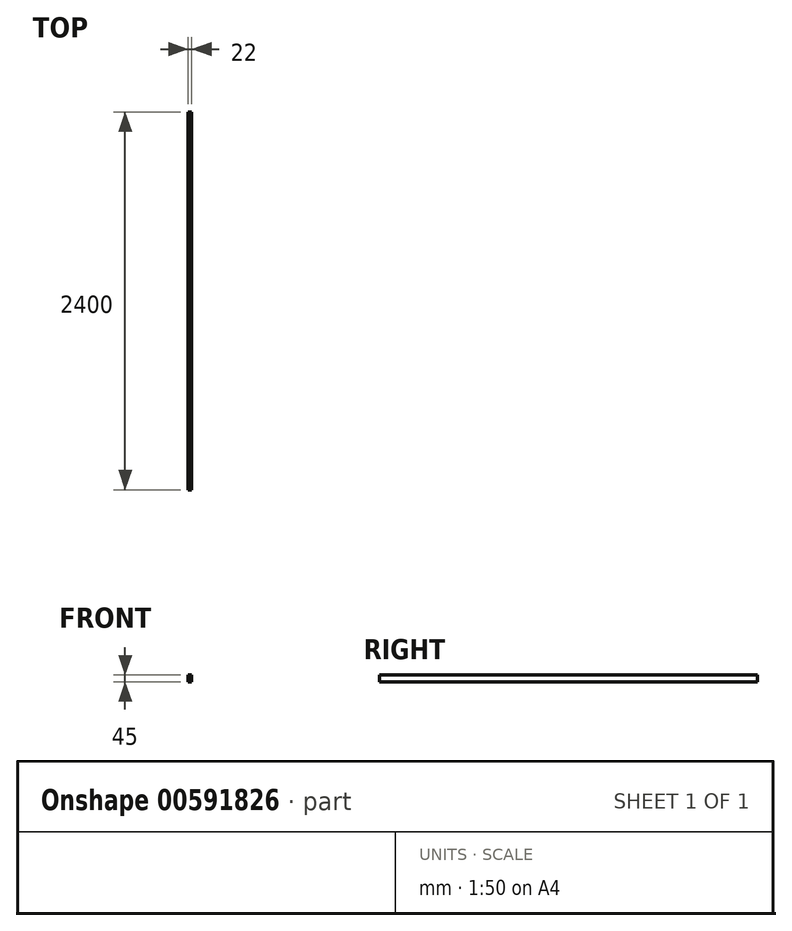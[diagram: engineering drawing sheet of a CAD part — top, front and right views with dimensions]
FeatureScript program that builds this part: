
annotation { "Feature Type Name" : "Feature", "Feature Type Description" : "" }
export const myFeature = defineFeature(function(context is Context, id is Id, definition is map)
    precondition{}
    {
        {
            var Q0;
            Q0=qCreatedBy(makeId("Front.planeOp"),FACE);
            var sketch = newSketch(context, id + "F0", { "sketchPlane" : qUnion([Q0])});
            skLineSegment(sketch, "E0.bottom", {"start": v(0, 0) * mm, "end": v(22, 0) * mm});
            skLineSegment(sketch, "E0.top", {"start": v(0, 45) * mm, "end": v(22, 45) * mm});
            skLineSegment(sketch, "E0.left", {"start": v(0, 0) * mm, "end": v(0, 45) * mm});
            skLineSegment(sketch, "E0.right", {"start": v(22, 0) * mm, "end": v(22, 45) * mm});
            skSolve(sketch);
        }
        {
            var Q0;
            Q0=qSketchRegion(id+"F0",true);
            extrude(context, id + "F1", {"entities" : qUnion([Q0]), "depth" : 2400 * mm, "offsetDistance" : 25 * mm});
        }
    });
